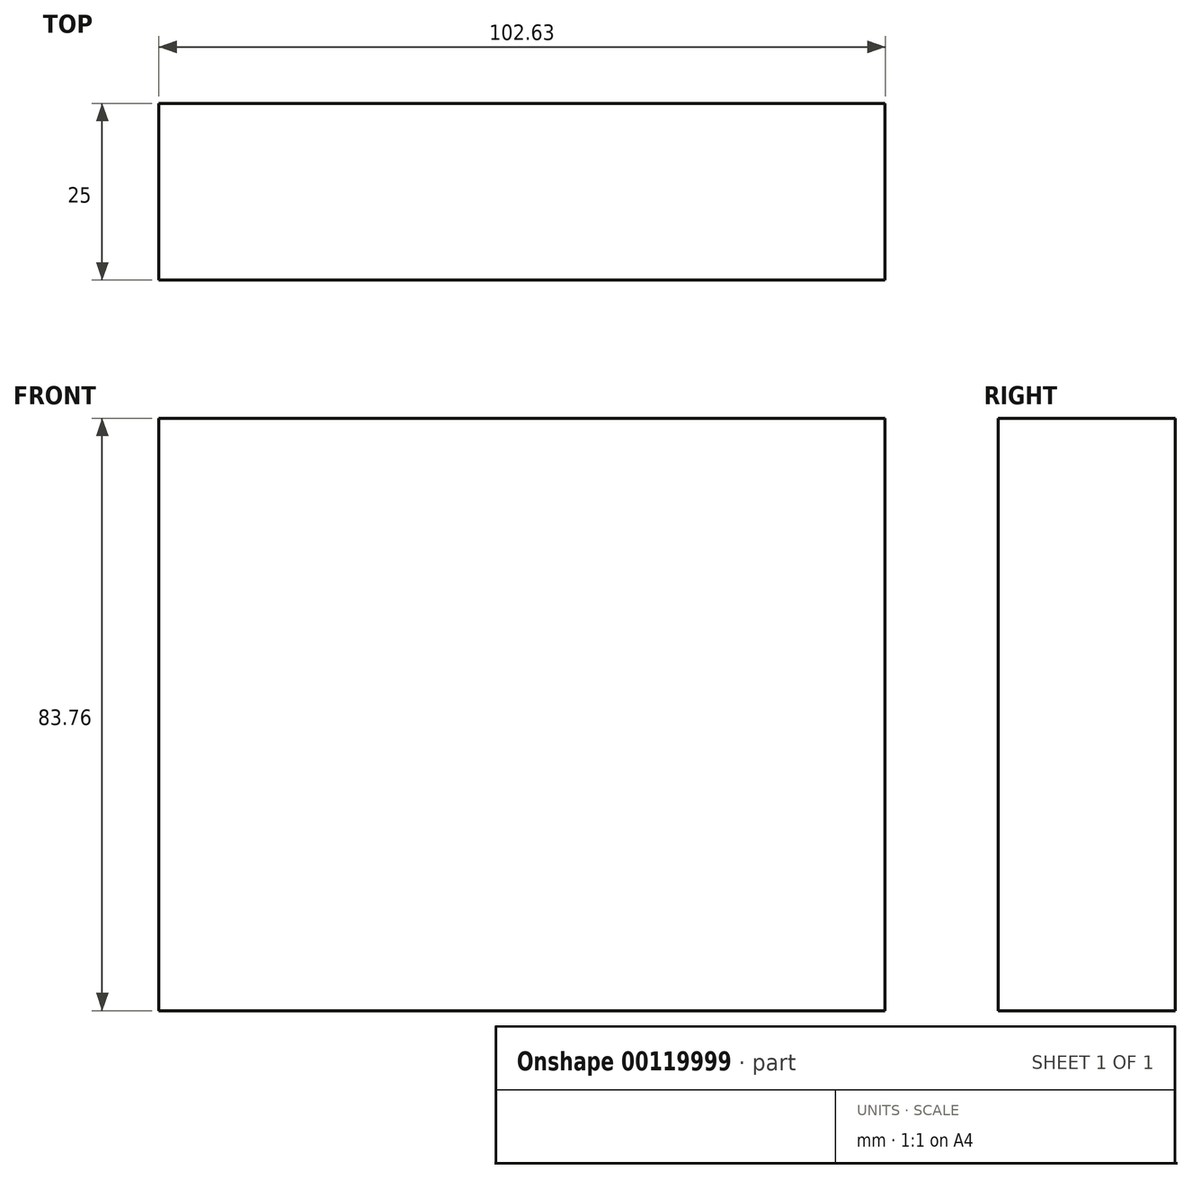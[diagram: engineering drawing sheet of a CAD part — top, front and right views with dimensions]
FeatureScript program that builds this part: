
annotation { "Feature Type Name" : "Feature", "Feature Type Description" : "" }
export const myFeature = defineFeature(function(context is Context, id is Id, definition is map)
    precondition{}
    {
        {
            var Q0;
            Q0=qCreatedBy(makeId("Front.planeOp"),FACE);
            var sketch = newSketch(context, id + "F0", { "sketchPlane" : qUnion([Q0])});
            skLineSegment(sketch, "E0.bottom", {"start": v(-63.67, 45.44) * mm, "end": v(38.96, 45.44) * mm});
            skLineSegment(sketch, "E0.top", {"start": v(-63.67, -38.32) * mm, "end": v(38.96, -38.32) * mm});
            skLineSegment(sketch, "E0.left", {"start": v(-63.67, 45.44) * mm, "end": v(-63.67, -38.32) * mm});
            skLineSegment(sketch, "E0.right", {"start": v(38.96, 45.44) * mm, "end": v(38.96, -38.32) * mm});
            skSolve(sketch);
        }
        {
            var Q0;
            Q0 = qSketchRegion(id + "F0", true);
            extrude(context, id + "F1", {"entities" : qUnion([Q0]), "depth" : 25 * mm});
        }
    });
